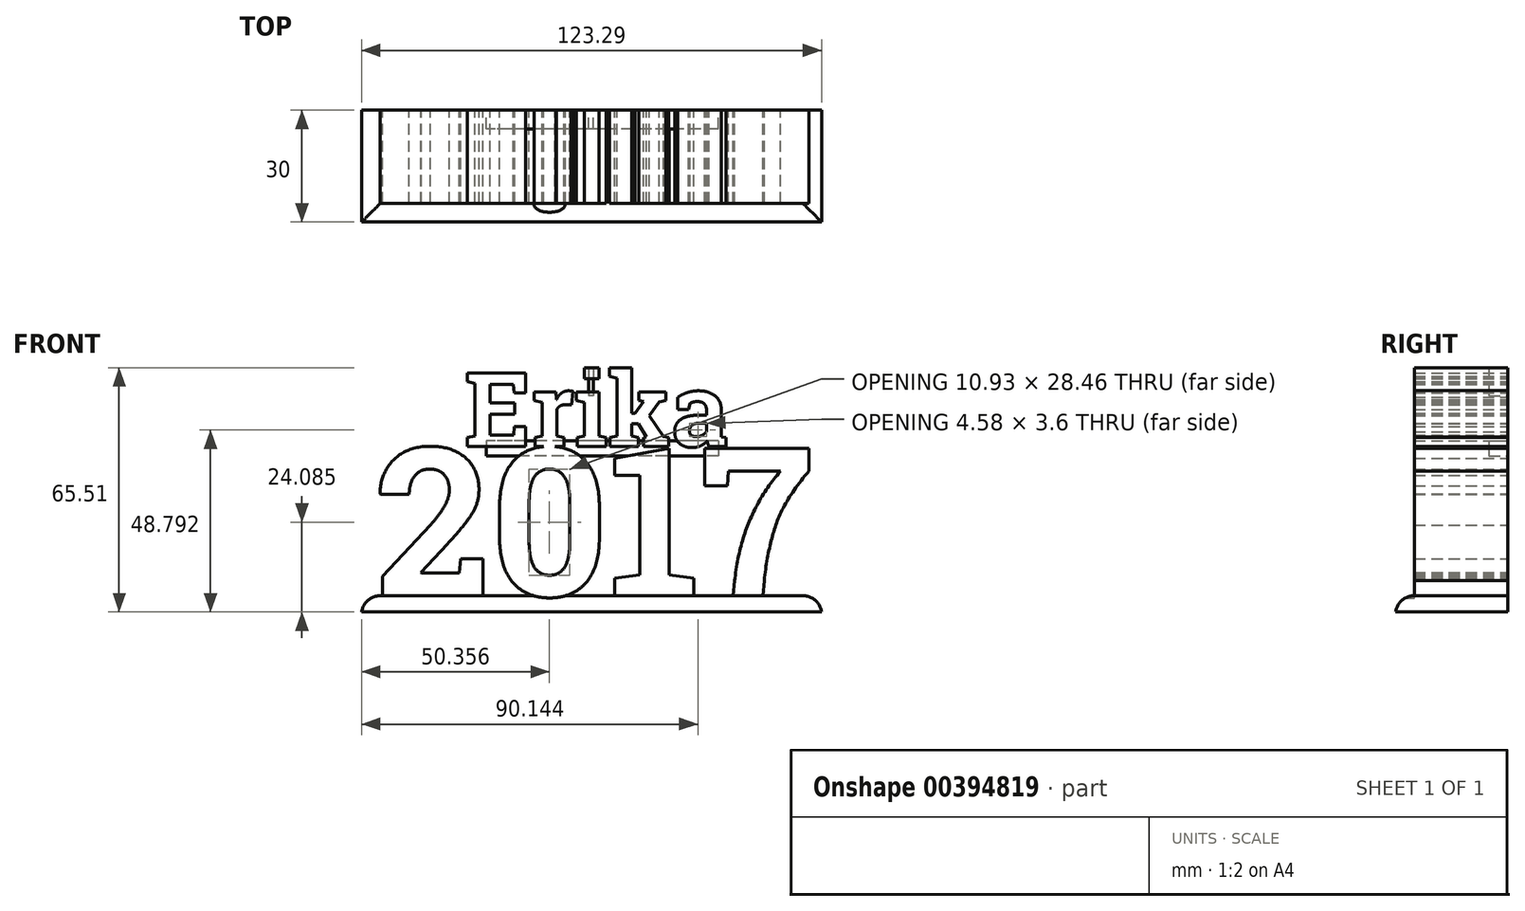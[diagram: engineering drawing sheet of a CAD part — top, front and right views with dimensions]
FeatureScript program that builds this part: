
annotation { "Feature Type Name" : "Feature", "Feature Type Description" : "" }
export const myFeature = defineFeature(function(context is Context, id is Id, definition is map)
    precondition{}
    {
        {
            var Q0;
            Q0=qCreatedBy(makeId("Front.planeOp"),FACE);
            var sketch = newSketch(context, id + "F0", { "sketchPlane" : qUnion([Q0])});
            skText(sketch, "E0", { "text": "2017", "fontName": "RobotoSlab-Bold.ttf"});
            skText(sketch, "E1", { "text": "Erika", "fontName": "RobotoSlab-Bold.ttf"});
            skLineSegment(sketch, "E2.bottom", {"start": v(59.82, -35.32) * mm, "end": v(-63.47, -35.32) * mm});
            skLineSegment(sketch, "E2.top", {"start": v(59.82, -39.67) * mm, "end": v(-63.47, -39.67) * mm});
            skLineSegment(sketch, "E2.left", {"start": v(59.82, -35.32) * mm, "end": v(59.82, -39.67) * mm});
            skLineSegment(sketch, "E2.right", {"start": v(-63.47, -35.32) * mm, "end": v(-63.47, -39.67) * mm});
            const initialGuessF0  = {"E0": [-0.05982, -0.03532, 1, 0, 0.04], "E1": [-0.0359, 0.00468, 1, 0, 0.02]};
            skSetInitialGuess(sketch, initialGuessF0);
            skSolve(sketch);
        }
        {
            var Q0;
            Q0 = qSketchRegion(id + "F0", true);
            var Q1;
            Q1=makeQuery(id+"F0.imprint","IMPRINT",FACE,{"disambiguationData":[TD([[makeQuery(id+"F0.imprint","IMPRINT",EDGE,{"derivedFrom":sQuery(id+"F0.wireOp",EDGE,"E0.sketch_text.stroke-43")}),-1.0]])]});
            var Q2;
            {var subQ0=sQuery(id+"F0.wireOp",EDGE,"E0.sketch_text.stroke-48");var subQ1=sQuery(id+"F0.wireOp",EDGE,"E0.sketch_text.stroke-47");var subQ2=makeQuery(id+"F0.imprint","INTERSECT",VERTEX,{"derivedFrom":[subQ1,subQ0]});Q2=makeQuery(id+"F0.imprint","IMPRINT",FACE,{"disambiguationData":[TD([[makeQuery(id+"F0.imprint","IMPRINT",EDGE,{"disambiguationData":[TD([[subQ2,1.0]])],"derivedFrom":subQ1}),-1.0]])]});}
            extrude(context, id + "F1", {"entities" : qUnion([Q0, Q1, Q2]), "depth" : 25 * mm});
        }
        {
            var Q0;
            Q0=makeQuery(id+"F0.imprint","IMPRINT",FACE,{"disambiguationData":[TD([[makeQuery(id+"F0.imprint","IMPRINT",EDGE,{"derivedFrom":sQuery(id+"F0.wireOp",EDGE,"E2.top")}),-1.0]])]});
            extrude(context, id + "F2", {"entities" : qUnion([Q0]), "operationType" : NewBodyOperationType.ADD, "depth" : 30 * mm});
        }
        {
            var Q0;
            {var subQ0=sQuery(id+"F0.wireOp",EDGE,"E2.right");var subQ1=sQuery(id+"F0.wireOp",EDGE,"E2.bottom");Q0=makeQuery(id+"F2.boolean.opBoolean","MERGE",EDGE,{"derivedFrom":[makeQuery(id+"F1.opExtrude","SWEPT_EDGE",EDGE,{"disambiguationData":[OSD([subQ1,subQ0])]}),makeQuery(id+"F2.opExtrude","SWEPT_EDGE",EDGE,{"disambiguationData":[OSD([subQ1,subQ0])]})]});}
            var Q1;
            {var subQ0=sQuery(id+"F0.wireOp",EDGE,"E2.bottom");var subQ1=makeQuery(id+"F0.imprint","INTERSECT",VERTEX,{"derivedFrom":[sQuery(id+"F0.wireOp",EDGE,"E0.sketch_text.stroke-0"),subQ0]});var subQ2=makeQuery(id+"F0.imprint","INTERSECT",VERTEX,{"derivedFrom":[sQuery(id+"F0.wireOp",EDGE,"E0.sketch_text.stroke-21"),subQ0]});Q1=makeQuery(id+"F2.opExtrude","CAP_EDGE",EDGE,{"disambiguationData":[OSD([subQ0]),TDD([makeQuery(id+"F0.imprint","IMPRINT",EDGE,{"disambiguationData":[TD([[subQ2,1.0]])],"derivedFrom":subQ0}),makeQuery(id+"F0.imprint","IMPRINT",EDGE,{"disambiguationData":[TD([[subQ1,1.0]])],"derivedFrom":subQ0}),makeQuery(id+"F0.imprint","IMPRINT",EDGE,{"disambiguationData":[TD([[subQ1,-1.0]])],"derivedFrom":subQ0})])],"isStart":false});}
            var Q2;
            {var subQ0=sQuery(id+"F0.wireOp",EDGE,"E2.left");var subQ1=sQuery(id+"F0.wireOp",EDGE,"E2.bottom");Q2=makeQuery(id+"F2.boolean.opBoolean","MERGE",EDGE,{"derivedFrom":[makeQuery(id+"F1.opExtrude","SWEPT_EDGE",EDGE,{"disambiguationData":[OSD([subQ1,subQ0])]}),makeQuery(id+"F2.opExtrude","SWEPT_EDGE",EDGE,{"disambiguationData":[OSD([subQ1,subQ0])]})]});}
            fillet(context, id + "F3", {"entities" : qUnion([Q0, Q1, Q2]), "radius" : 5 * mm, "tangentPropagation" : true, "allowEdgeOverflow" : false});
        }
        {
            var Q0;
            {var subQ35=sQuery(id+"F0.wireOp",EDGE,"E1.sketch_text.stroke-48");Q0=makeQuery(id+"F0.imprint","IMPRINT",FACE,{"disambiguationData":[TD([[makeQuery(id+"F0.imprint","IMPRINT",EDGE,{"derivedFrom":subQ35}),1.0]])]});}
            var Q1;
            {var subQ10=sQuery(id+"F0.wireOp",EDGE,"E0.sketch_text.stroke-29");var subQ12=sQuery(id+"F0.wireOp",EDGE,"4ejI8ieE-HNRa-zXMR-NTKY-f4UQnyzIwvmO.top");var subQ13=makeQuery(id+"F0.imprint","INTERSECT",VERTEX,{"derivedFrom":[subQ10,subQ12]});Q1=makeQuery(id+"F0.imprint","IMPRINT",FACE,{"disambiguationData":[TD([[makeQuery(id+"F0.imprint","IMPRINT",EDGE,{"disambiguationData":[TD([[subQ13,-1.0]])],"derivedFrom":subQ10}),1.0]])]});}
            extrude(context, id + "F4", {"entities" : qUnion([Q0, Q1]), "operationType" : NewBodyOperationType.ADD, "depth" : 5 * mm});
        }
        {
            var Q0;
            Q0=makeQuery(id+"F0.imprint","IMPRINT",FACE,{"disambiguationData":[TD([[makeQuery(id+"F0.imprint","IMPRINT",EDGE,{"derivedFrom":sQuery(id+"F0.wireOp",EDGE,"E1.sketch_text.stroke-54")}),-1.0]])]});
            var sketch = newSketch(context, id + "F5", { "sketchPlane" : qUnion([Q0])});
            skLineSegment(sketch, "E3.bottom", {"start": v(32.14, 6.2) * mm, "end": v(-30.03, 6.2) * mm});
            skLineSegment(sketch, "E3.top", {"start": v(32.14, 2.16) * mm, "end": v(-30.03, 2.16) * mm});
            skLineSegment(sketch, "E3.left", {"start": v(32.14, 6.2) * mm, "end": v(32.14, 2.16) * mm});
            skLineSegment(sketch, "E3.right", {"start": v(-30.03, 6.2) * mm, "end": v(-30.03, 2.16) * mm});
            skLineSegment(sketch, "E4.bottom", {"start": v(-1.4, 25.68) * mm, "end": v(-2.6, 25.68) * mm});
            skLineSegment(sketch, "E4.top", {"start": v(-1.4, 18.32) * mm, "end": v(-2.6, 18.32) * mm});
            skLineSegment(sketch, "E4.left", {"start": v(-1.4, 25.68) * mm, "end": v(-1.4, 18.32) * mm});
            skLineSegment(sketch, "E4.right", {"start": v(-2.6, 25.68) * mm, "end": v(-2.6, 18.32) * mm});
            skSolve(sketch);
        }
        {
            var Q0;
            Q0 = qSketchRegion(id + "F5", true);
            extrude(context, id + "F6", {"entities" : qUnion([Q0]), "depth" : 5 * mm});
        }
    });
